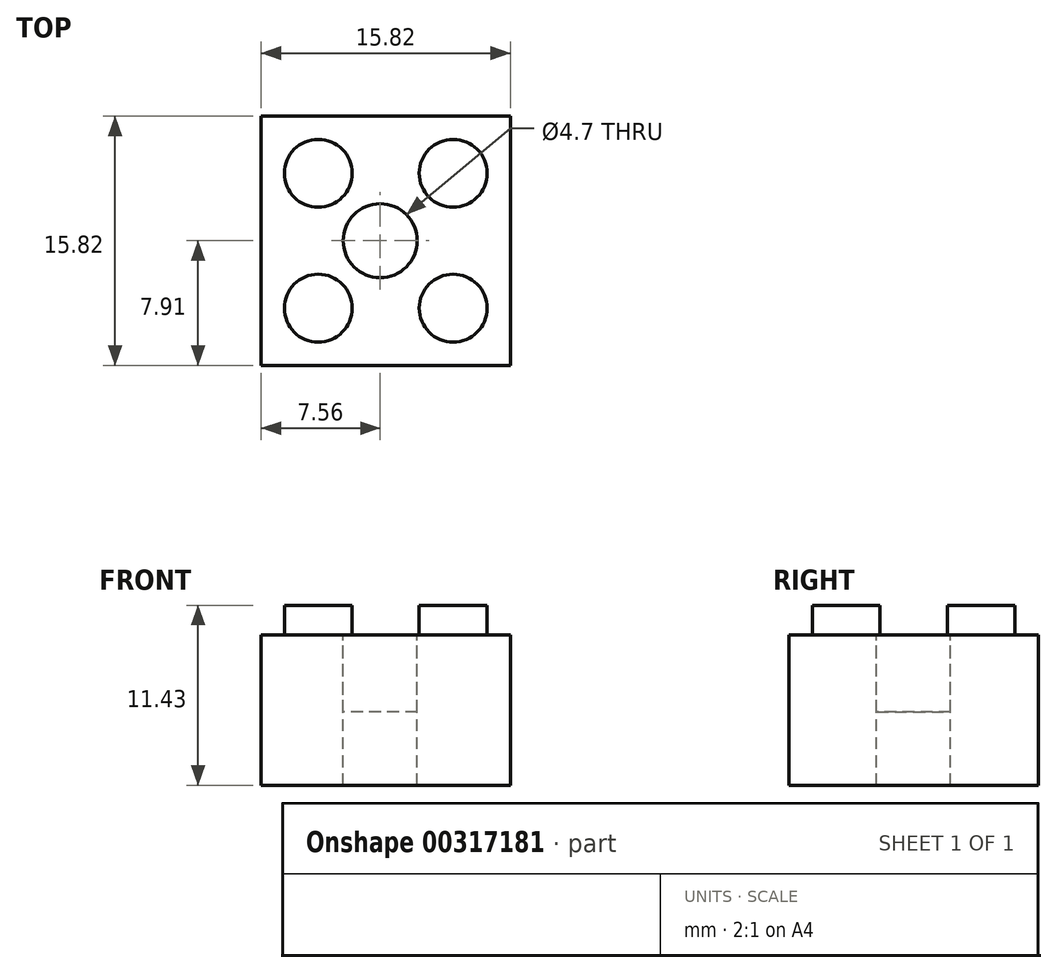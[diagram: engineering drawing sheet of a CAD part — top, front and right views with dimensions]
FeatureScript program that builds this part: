
annotation { "Feature Type Name" : "Feature", "Feature Type Description" : "" }
export const myFeature = defineFeature(function(context is Context, id is Id, definition is map)
    precondition{}
    {
        {
            var Q0;
            Q0=qCreatedBy(makeId("Top.planeOp"),FACE);
            var sketch = newSketch(context, id + "F0", { "sketchPlane" : qUnion([Q0])});
            skLineSegment(sketch, "E0.bottom", {"start": v(-7.56, 7.9) * mm, "end": v(8.26, 7.9) * mm});
            skLineSegment(sketch, "E0.top", {"start": v(-7.56, -7.9) * mm, "end": v(8.26, -7.9) * mm});
            skLineSegment(sketch, "E0.left", {"start": v(-7.56, 7.9) * mm, "end": v(-7.56, -7.9) * mm});
            skLineSegment(sketch, "E0.right", {"start": v(8.26, 7.9) * mm, "end": v(8.26, -7.9) * mm});
            skPoint(sketch, "E0.middle", {"position": v(0.35, 0) * mm});
            skCircle(sketch, "E1", {"center": v(-3.93, 4.29) * mm, "radius": 2.15 * mm});
            skCircle(sketch, "E2", {"center": v(-3.93, -4.29) * mm, "radius": 2.15 * mm});
            skCircle(sketch, "E3", {"center": v(4.64, -4.29) * mm, "radius": 2.15 * mm});
            skCircle(sketch, "E4", {"center": v(4.64, 4.29) * mm, "radius": 2.15 * mm});
            skCircle(sketch, "E5", {"center": v(0, 0) * mm, "radius": 2.35 * mm});
            skSolve(sketch);
        }
        {
            var Q0;
            Q0=makeQuery(id+"F0.imprint","IMPRINT",FACE,{"disambiguationData":[TD([[makeQuery(id+"F0.imprint","IMPRINT",EDGE,{"derivedFrom":sQuery(id+"F0.wireOp",EDGE,"E0.bottom")}),-1.0]])]});
            var Q1;
            Q1=makeQuery(id+"F0.imprint","IMPRINT",FACE,{"disambiguationData":[TD([[makeQuery(id+"F0.imprint","IMPRINT",EDGE,{"derivedFrom":sQuery(id+"F0.wireOp",EDGE,"E2")}),1.0]])]});
            var Q2;
            Q2=makeQuery(id+"F0.imprint","IMPRINT",FACE,{"disambiguationData":[TD([[makeQuery(id+"F0.imprint","IMPRINT",EDGE,{"derivedFrom":sQuery(id+"F0.wireOp",EDGE,"E1")}),1.0]])]});
            var Q3;
            Q3=makeQuery(id+"F0.imprint","IMPRINT",FACE,{"disambiguationData":[TD([[makeQuery(id+"F0.imprint","IMPRINT",EDGE,{"derivedFrom":sQuery(id+"F0.wireOp",EDGE,"E4")}),1.0]])]});
            var Q4;
            Q4=makeQuery(id+"F0.imprint","IMPRINT",FACE,{"disambiguationData":[TD([[makeQuery(id+"F0.imprint","IMPRINT",EDGE,{"derivedFrom":sQuery(id+"F0.wireOp",EDGE,"E3")}),1.0]])]});
            extrude(context, id + "F1", {"entities" : qUnion([Q0, Q1, Q2, Q3, Q4]), "oppositeDirection" : true, "depth" : 9.55 * mm});
        }
        {
            var Q0;
            Q0=makeQuery(id+"F0.imprint","IMPRINT",FACE,{"disambiguationData":[TD([[makeQuery(id+"F0.imprint","IMPRINT",EDGE,{"derivedFrom":sQuery(id+"F0.wireOp",EDGE,"E1")}),1.0]])]});
            var Q1;
            Q1=makeQuery(id+"F0.imprint","IMPRINT",FACE,{"disambiguationData":[TD([[makeQuery(id+"F0.imprint","IMPRINT",EDGE,{"derivedFrom":sQuery(id+"F0.wireOp",EDGE,"E2")}),1.0]])]});
            var Q2;
            Q2=makeQuery(id+"F0.imprint","IMPRINT",FACE,{"disambiguationData":[TD([[makeQuery(id+"F0.imprint","IMPRINT",EDGE,{"derivedFrom":sQuery(id+"F0.wireOp",EDGE,"E4")}),1.0]])]});
            var Q3;
            Q3=makeQuery(id+"F0.imprint","IMPRINT",FACE,{"disambiguationData":[TD([[makeQuery(id+"F0.imprint","IMPRINT",EDGE,{"derivedFrom":sQuery(id+"F0.wireOp",EDGE,"E3")}),1.0]])]});
            extrude(context, id + "F2", {"entities" : qUnion([Q0, Q1, Q2, Q3]), "depth" : 1.88 * mm});
        }
        {
            var Q0;
            Q0=makeQuery(id+"F0.imprint","IMPRINT",FACE,{"disambiguationData":[TD([[makeQuery(id+"F0.imprint","IMPRINT",EDGE,{"derivedFrom":sQuery(id+"F0.wireOp",EDGE,"E5")}),1.0]])]});
            extrude(context, id + "F3", {"entities" : qUnion([Q0]), "oppositeDirection" : true, "depth" : 4.88 * mm});
        }
    });
